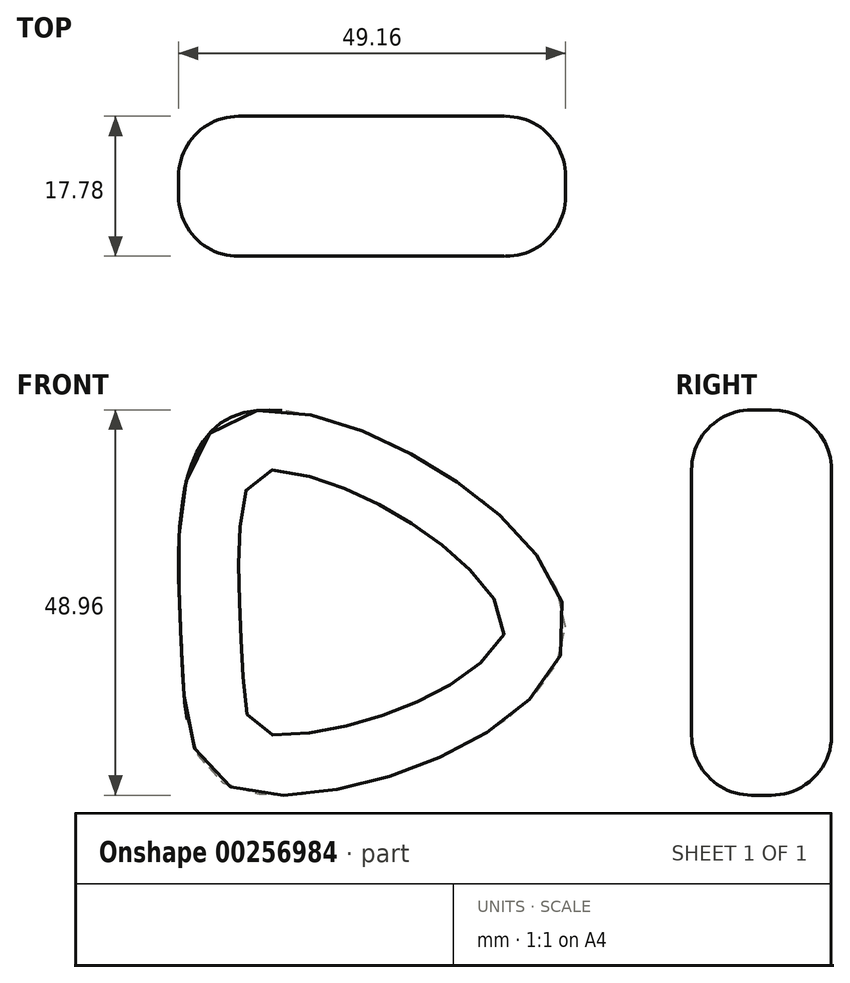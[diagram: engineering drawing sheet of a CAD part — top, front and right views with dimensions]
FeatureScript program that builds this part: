
annotation { "Feature Type Name" : "Feature", "Feature Type Description" : "" }
export const myFeature = defineFeature(function(context is Context, id is Id, definition is map)
    precondition{}
    {
        {
            var Q0;
            Q0=qCreatedBy(makeId("Front.planeOp"),FACE);
            var sketch = newSketch(context, id + "F0", { "sketchPlane" : qUnion([Q0])});
            skFitSpline(sketch, "E0", {"points": [v(-48.83, 0) * mm, v(-40.95, 29.13) * mm, v(0, 1.37) * mm, v(-40.6, -19.02) * mm, v(-48.83, 0) * mm]});
            skSolve(sketch);
        }
        {
            var Q0;
            Q0=makeQuery(id+"F0.imprint","IMPRINT",FACE,{"disambiguationData":[TD([[makeQuery(id+"F0.imprint","IMPRINT",EDGE,{"derivedFrom":sQuery(id+"F0.wireOp",EDGE,"E0")}),-1.0]])]});
            extrude(context, id + "F1", {"entities" : qUnion([Q0]), "depth" : 17.78 * mm});
        }
        {
            var Q0;
            Q0=makeQuery(id+"F1.opExtrude","CAP_EDGE",EDGE,{"disambiguationData":[OSD([sQuery(id+"F0.wireOp",EDGE,"E0")])],"isStart":false});
            var Q1;
            Q1=makeQuery(id+"F1.opExtrude","SWEPT_FACE",FACE,{"disambiguationData":[OSD([sQuery(id+"F0.wireOp",EDGE,"E0")])]});
            fillet(context, id + "F2", {"entities" : qUnion([Q0, Q1]), "radius" : 7.62 * mm, "tangentPropagation" : true, "allowEdgeOverflow" : false});
        }
    });
